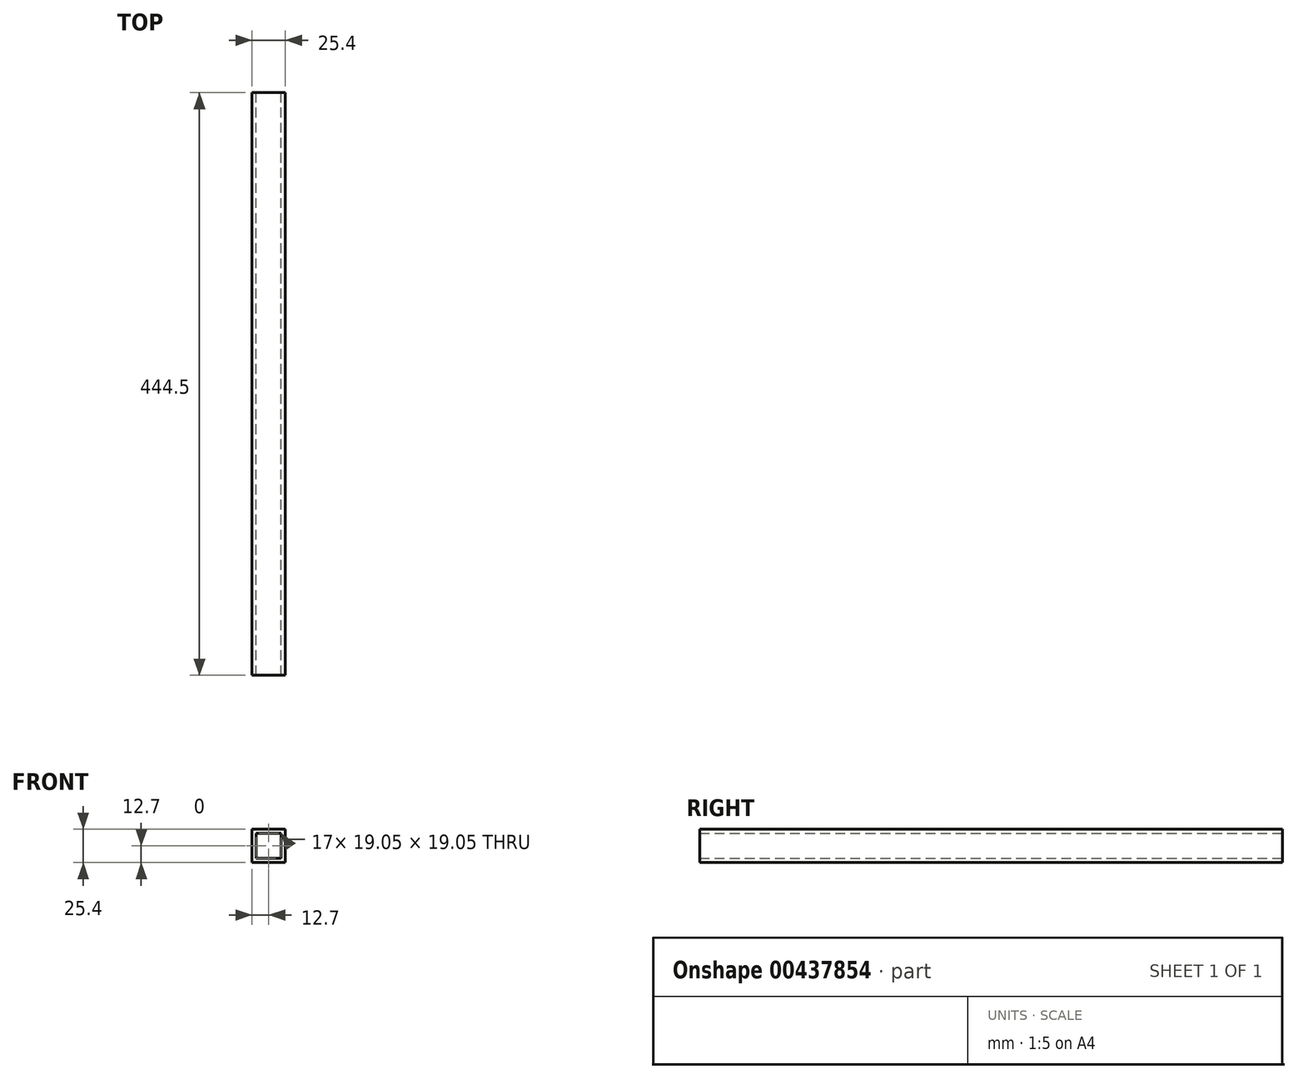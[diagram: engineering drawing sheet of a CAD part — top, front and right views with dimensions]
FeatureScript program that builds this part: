
annotation { "Feature Type Name" : "Feature", "Feature Type Description" : "" }
export const myFeature = defineFeature(function(context is Context, id is Id, definition is map)
    precondition{}
    {
        {
            var Q0;
            Q0=qCreatedBy(makeId("Front.planeOp"),FACE);
            var sketch = newSketch(context, id + "F0", { "sketchPlane" : qUnion([Q0])});
            skLineSegment(sketch, "E0.bottom", {"start": v(-12.7, 12.7) * mm, "end": v(12.7, 12.7) * mm});
            skLineSegment(sketch, "E0.top", {"start": v(-12.7, -12.7) * mm, "end": v(12.7, -12.7) * mm});
            skLineSegment(sketch, "E0.left", {"start": v(-12.7, 12.7) * mm, "end": v(-12.7, -12.7) * mm});
            skLineSegment(sketch, "E0.right", {"start": v(12.7, 12.7) * mm, "end": v(12.7, -12.7) * mm});
            skLineSegment(sketch, "E1.bottom", {"start": v(-9.52, 9.52) * mm, "end": v(9.53, 9.52) * mm});
            skLineSegment(sketch, "E1.top", {"start": v(-9.52, -9.52) * mm, "end": v(9.53, -9.52) * mm});
            skLineSegment(sketch, "E1.left", {"start": v(-9.52, 9.52) * mm, "end": v(-9.52, -9.52) * mm});
            skLineSegment(sketch, "E1.right", {"start": v(9.53, 9.52) * mm, "end": v(9.53, -9.52) * mm});
            skSolve(sketch);
        }
        {
            var Q0;
            Q0=makeQuery(id+"F0.imprint","IMPRINT",FACE,{"disambiguationData":[TD([[makeQuery(id+"F0.imprint","IMPRINT",EDGE,{"derivedFrom":sQuery(id+"F0.wireOp",EDGE,"E0.bottom")}),-1.0]])]});
            extrude(context, id + "F1", {"entities" : qUnion([Q0]), "depth" : 444.5 * mm});
        }
    });
